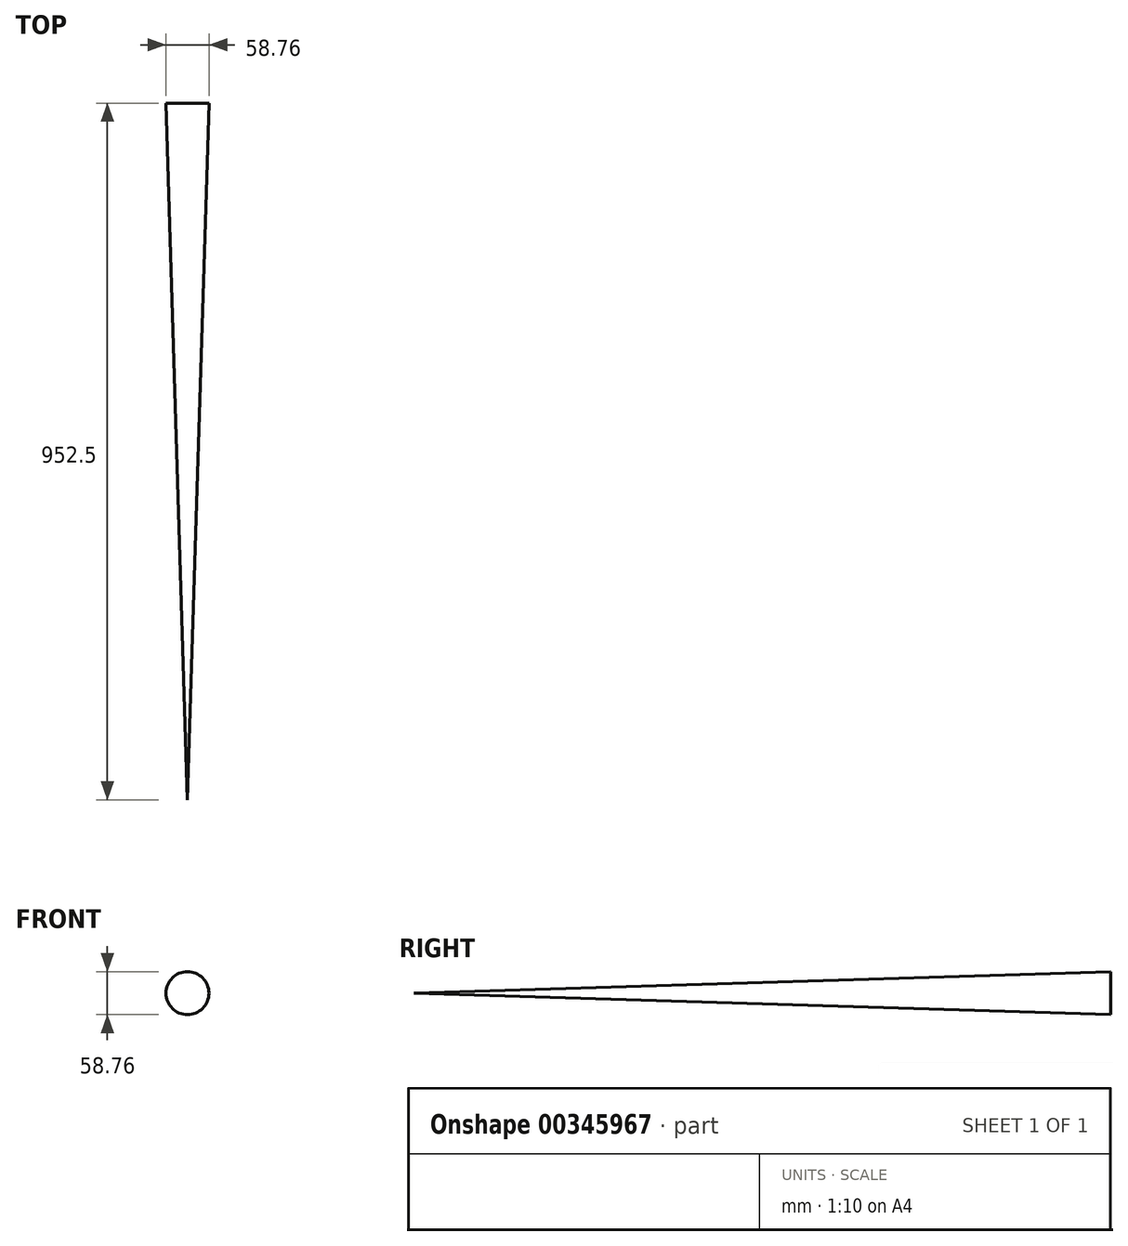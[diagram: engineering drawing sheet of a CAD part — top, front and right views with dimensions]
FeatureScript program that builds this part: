
annotation { "Feature Type Name" : "Feature", "Feature Type Description" : "" }
export const myFeature = defineFeature(function(context is Context, id is Id, definition is map)
    precondition{}
    {
        {
            var Q0;
            Q0=qCreatedBy(makeId("Front.planeOp"),FACE);
            var sketch = newSketch(context, id + "F0", { "sketchPlane" : qUnion([Q0])});
            skCircle(sketch, "E0", {"center": v(0, 0) * mm, "radius": 29.38 * mm});
            skSolve(sketch);
        }
        {
            var Q0;
            Q0=qCreatedBy(makeId("Front.planeOp"),FACE);
            cPlane(context, id + "F1", {"entities" : qUnion([Q0]), "cplaneType" : CPlaneType.OFFSET, "offset" : 952.5 * mm, "width" : 152.4 * mm, "height" : 152.4 * mm});
        }
        {
            var Q0;
            Q0=qCreatedBy(id+"F1.planeOp",FACE);
            var sketch = newSketch(context, id + "F2", { "sketchPlane" : qUnion([Q0])});
            skCircle(sketch, "E1", {"center": v(0, 0) * mm, "radius": 0.01 * mm});
            skSolve(sketch);
        }
        {
            var Q0;
            Q0=makeQuery(id+"F0.imprint","IMPRINT",FACE,{"disambiguationData":[TD([[makeQuery(id+"F0.imprint","IMPRINT",EDGE,{"derivedFrom":sQuery(id+"F0.wireOp",EDGE,"E0")}),1.0]])]});
            var Q1;
            Q1=sQuery(id+"F2.wireOp",VERTEX,"E1.center");
            loft(context, id + "F3", {"sheetProfilesArray" : [{ "sheetProfileEntities" : qUnion([Q0]) }, { "sheetProfileEntities" : qUnion([Q1]) }]});
        }
    });
